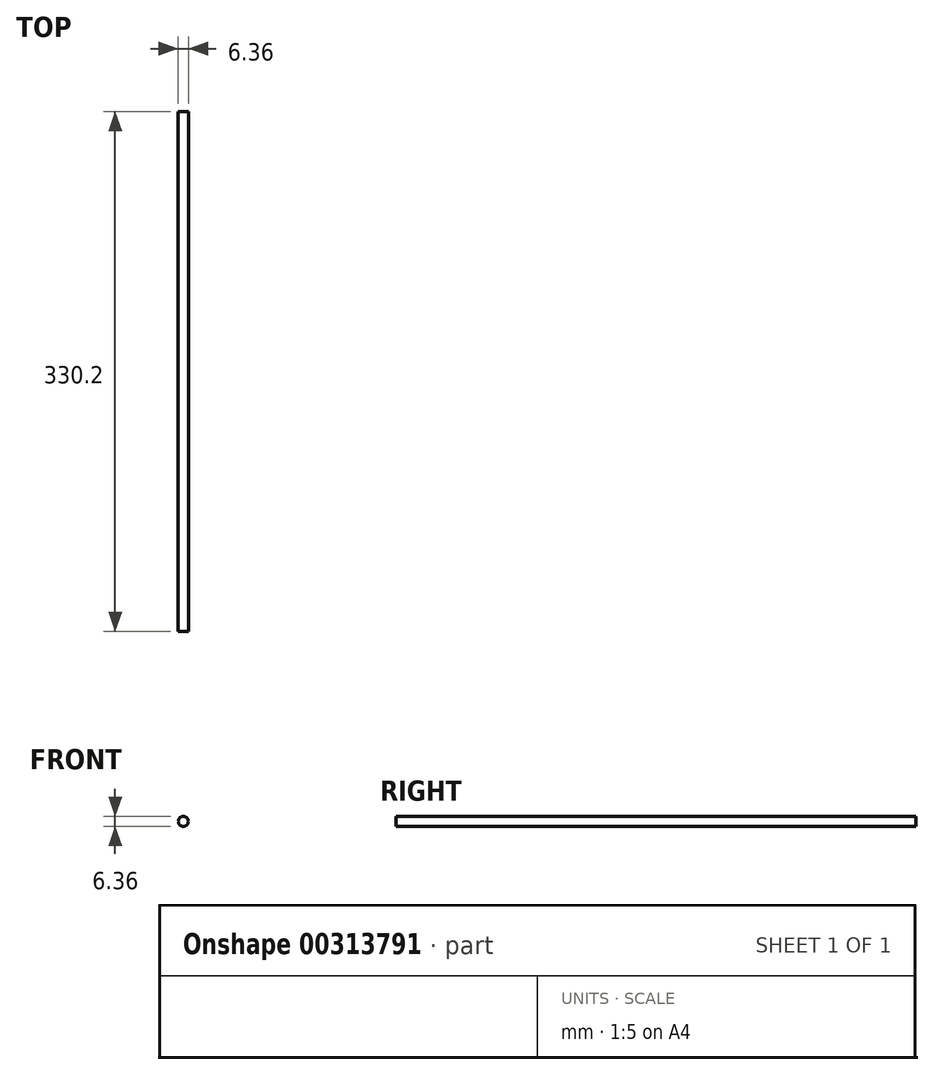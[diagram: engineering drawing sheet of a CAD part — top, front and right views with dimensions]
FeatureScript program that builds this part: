
annotation { "Feature Type Name" : "Feature", "Feature Type Description" : "" }
export const myFeature = defineFeature(function(context is Context, id is Id, definition is map)
    precondition{}
    {
        {
            var Q0;
            Q0=qCreatedBy(makeId("Front.planeOp"),FACE);
            var sketch = newSketch(context, id + "F0", { "sketchPlane" : qUnion([Q0])});
            skCircle(sketch, "E0", {"center": v(0, 0) * mm, "radius": 3.18 * mm});
            skSolve(sketch);
        }
        {
            var Q0;
            Q0=makeQuery(id+"F0.imprint","IMPRINT",FACE,{"disambiguationData":[TD([[makeQuery(id+"F0.imprint","IMPRINT",EDGE,{"derivedFrom":sQuery(id+"F0.wireOp",EDGE,"E0")}),1.0]])]});
            extrude(context, id + "F1", {"entities" : qUnion([Q0]), "endBound" : BoundingType.SYMMETRIC, "depth" : 330.2 * mm});
        }
    });
